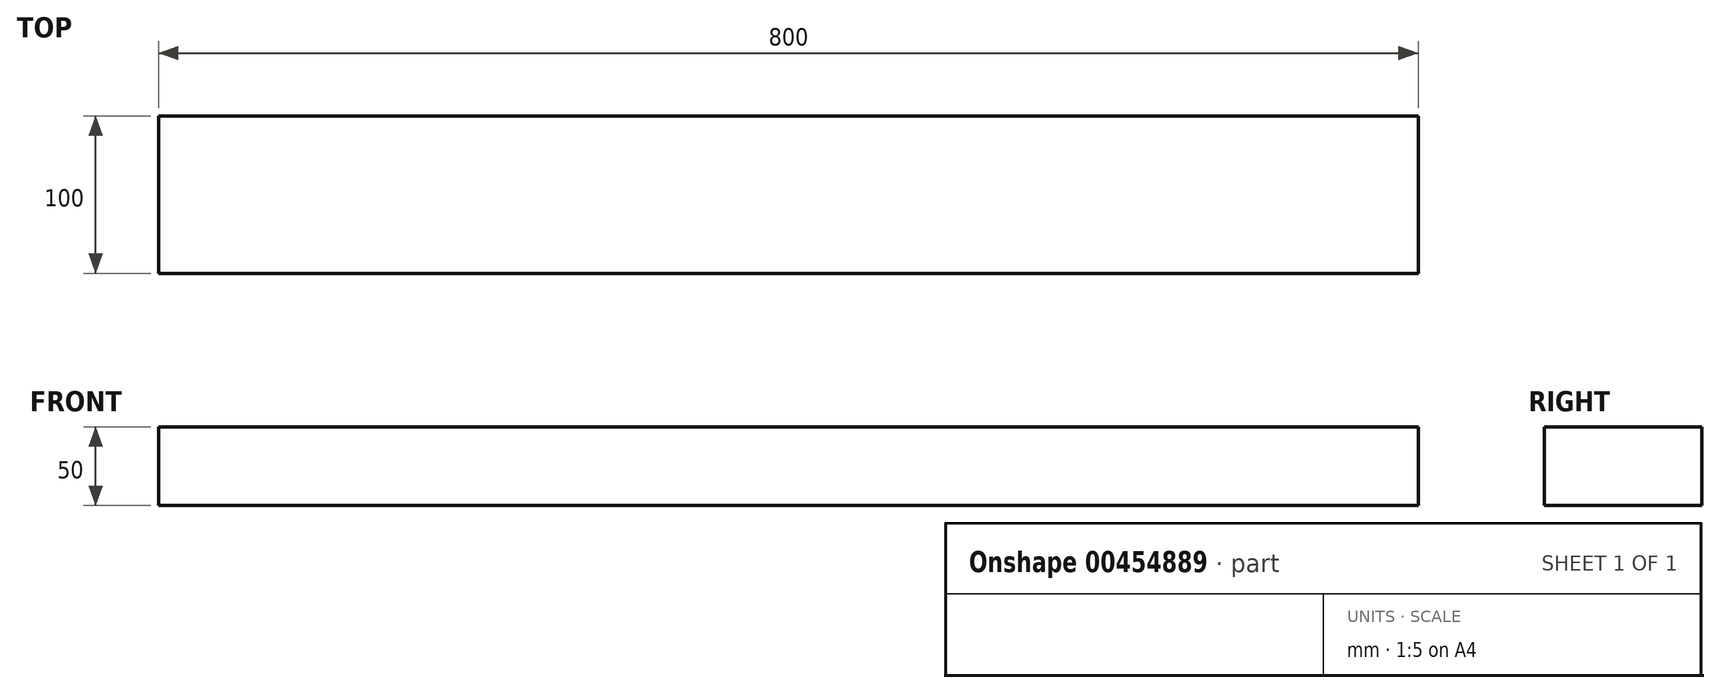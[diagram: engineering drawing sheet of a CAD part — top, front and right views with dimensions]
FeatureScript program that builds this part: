
annotation { "Feature Type Name" : "Feature", "Feature Type Description" : "" }
export const myFeature = defineFeature(function(context is Context, id is Id, definition is map)
    precondition{}
    {
        {
            var Q0;
            Q0=qCreatedBy(makeId("Right.planeOp"),FACE);
            var sketch = newSketch(context, id + "F0", { "sketchPlane" : qUnion([Q0])});
            skLineSegment(sketch, "E0.bottom", {"start": v(0, 0) * mm, "end": v(100, 0) * mm});
            skLineSegment(sketch, "E0.top", {"start": v(0, 50) * mm, "end": v(100, 50) * mm});
            skLineSegment(sketch, "E0.left", {"start": v(0, 0) * mm, "end": v(0, 50) * mm});
            skLineSegment(sketch, "E0.right", {"start": v(100, 0) * mm, "end": v(100, 50) * mm});
            skSolve(sketch);
        }
        {
            var Q0;
            Q0 = qSketchRegion(id + "F0", true);
            extrude(context, id + "F1", {"entities" : qUnion([Q0]), "depth" : 800 * mm});
        }
    });
